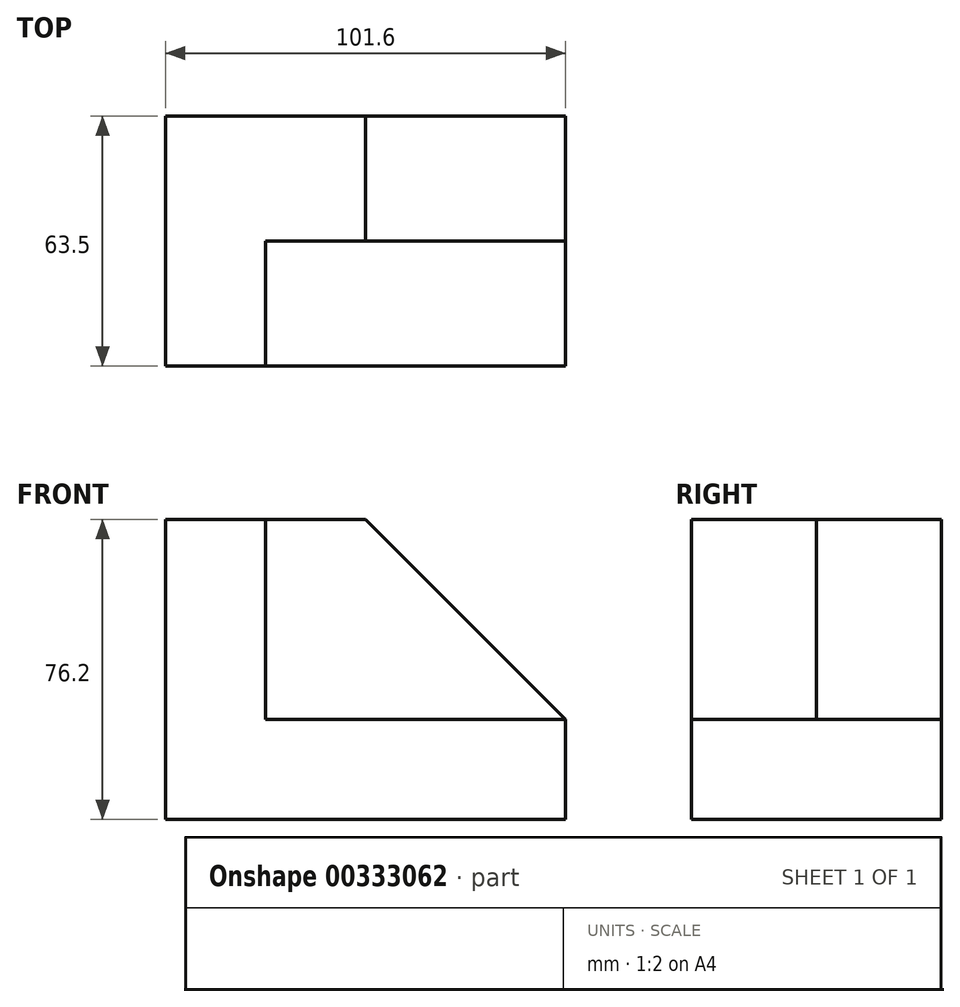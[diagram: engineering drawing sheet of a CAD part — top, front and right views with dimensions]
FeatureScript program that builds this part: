
annotation { "Feature Type Name" : "Feature", "Feature Type Description" : "" }
export const myFeature = defineFeature(function(context is Context, id is Id, definition is map)
    precondition{}
    {
        {
            var Q0;
            Q0=qCreatedBy(makeId("Front.planeOp"),FACE);
            var sketch = newSketch(context, id + "F0", { "sketchPlane" : qUnion([Q0])});
            skLineSegment(sketch, "E0", {"start": v(-54.51, 20.57) * mm, "end": v(-54.51, -55.63) * mm});
            skLineSegment(sketch, "E1", {"start": v(-54.51, -55.63) * mm, "end": v(47.09, -55.63) * mm});
            skLineSegment(sketch, "E2", {"start": v(47.09, -55.63) * mm, "end": v(47.09, -30.23) * mm});
            skLineSegment(sketch, "E3", {"start": v(47.09, -30.23) * mm, "end": v(-29.11, -30.23) * mm});
            skLineSegment(sketch, "E4", {"start": v(-29.11, -30.23) * mm, "end": v(-29.11, 20.57) * mm});
            skLineSegment(sketch, "E5", {"start": v(-29.11, 20.57) * mm, "end": v(-54.51, 20.57) * mm});
            skSolve(sketch);
        }
        {
            var Q0;
            Q0=makeQuery(id+"F0.imprint","IMPRINT",FACE,{"disambiguationData":[TD([[makeQuery(id+"F0.imprint","IMPRINT",EDGE,{"derivedFrom":sQuery(id+"F0.wireOp",EDGE,"E0")}),1.0]])]});
            extrude(context, id + "F1", {"entities" : qUnion([Q0]), "depth" : 63.5 * mm});
        }
        {
            var Q0;
            Q0=makeQuery(id+"F1.opExtrude","SWEPT_FACE",FACE,{"disambiguationData":[OSD([sQuery(id+"F0.wireOp",EDGE,"E3")])]});
            var sketch = newSketch(context, id + "F2", { "sketchPlane" : qUnion([Q0])});
            skLineSegment(sketch, "E6.bottom", {"start": v(-29.11, 0) * mm, "end": v(47.09, 0) * mm});
            skLineSegment(sketch, "E6.top", {"start": v(-29.11, -31.75) * mm, "end": v(47.09, -31.75) * mm});
            skLineSegment(sketch, "E6.left", {"start": v(-29.11, 0) * mm, "end": v(-29.11, -31.75) * mm});
            skLineSegment(sketch, "E6.right", {"start": v(47.09, 0) * mm, "end": v(47.09, -31.75) * mm});
            skSolve(sketch);
        }
        {
            var Q0;
            Q0=makeQuery(id+"F2.imprint","IMPRINT",FACE,{"disambiguationData":[TD([[makeQuery(id+"F2.imprint","IMPRINT",EDGE,{"derivedFrom":sQuery(id+"F2.wireOp",EDGE,"E6.bottom")}),1.0]])]});
            extrude(context, id + "F3", {"entities" : qUnion([Q0]), "operationType" : NewBodyOperationType.ADD, "depth" : 50.8 * mm});
        }
        {
            var Q0;
            Q0=makeQuery(id+"F3.opExtrude","CAP_EDGE",EDGE,{"disambiguationData":[OSD([sQuery(id+"F2.wireOp",EDGE,"E6.right")])],"isStart":false});
            chamfer(context, id + "F4", {"entities" : qUnion([Q0]), "width" : 50.8 * mm, "tangentPropagation" : true});
        }
    });
